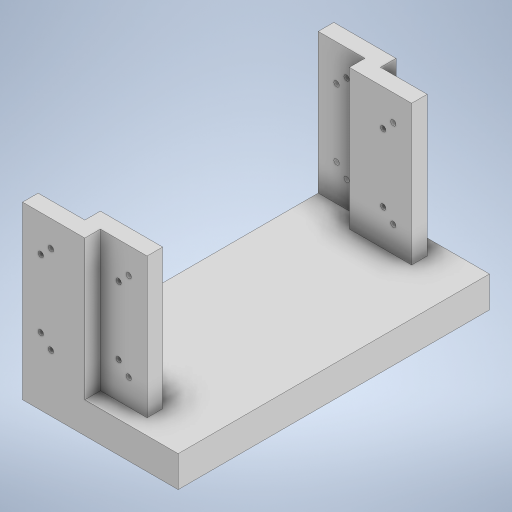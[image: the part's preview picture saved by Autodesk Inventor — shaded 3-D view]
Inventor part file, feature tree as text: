
AUTODESK INVENTOR PART (.ipt)
format: ipt  version: 2023 (Build 270158000, 158)  size: 315,392 bytes
history: native  units: mm
features: sketch x6, extrude x4, hole x2, other x1, mirror x1
ambient origin geometry x8: Origin, YZ Plane, XZ Plane, XY Plane, X Axis, Y Axis, Z Axis, Center Point
bodies: Body1 (feature_tree)
feature tree (14):
  other  "Sólido1"
  extrude  "Extrusión1"  Depth=90.0mm
  hole  "Agujero1"  [1 undecoded]
  extrude  "Extrusión2"  TaperAngle=0.0deg  [1 undecoded]
  extrude  "Extrusión3"  Depth=90.0mm
  hole  "Agujero2"  [1 undecoded]
  extrude  "Extrusión4"  Depth=90.0mm
  mirror  "Simetría1"
  sketch  "Boceto1"  dims[d0=30.0mm d1=90.0mm]
  sketch  "Boceto2"  dims[d2=10.0mm d3=0.0mm]
  sketch  "Boceto3"  dims[d4=1.75mm d5=1.75mm d6=1.75mm d7=1.75mm d8=10.0mm d9=10.0mm d10=10.0mm d11=15.0mm d12=0.0mm]
  sketch  "Boceto4"  dims[d13=30.0mm d14=0.0mm]
  sketch  "Boceto5"  dims[d15=90.0mm d16=15.0mm]
  sketch  "Boceto6"  dims[d17=3.5mm d18=6.0mm d19=4.0mm d20=2.0mm d21=90.0deg d22=8.0mm d23=20.594885mm d24=20.0mm d25=90.0mm d26=10.0mm d27=0.0mm d28=30.0mm d29=0.0mm d30=3.5mm d31=1.75mm d32=1.75mm d33=1.75mm d34=1.75mm d35=10.0mm d36=10.0mm d38=10.0mm d39=-41.10961mm d40=15.0mm d41=0.0mm d42=15.0mm d43=90.0mm d45=0.0mm d46=3.5mm d47=6.0mm d48=4.0mm d49=2.0mm d50=90.0deg d51=8.0mm d52=20.594885mm d53=20.0mm d54=100.0mm d55=0.0mm]
note: 3 required parameter values undecoded (feature->parameter linkage not recoverable at this tier; creation-order binding heuristic only, values carry confidence <= 0.55)
